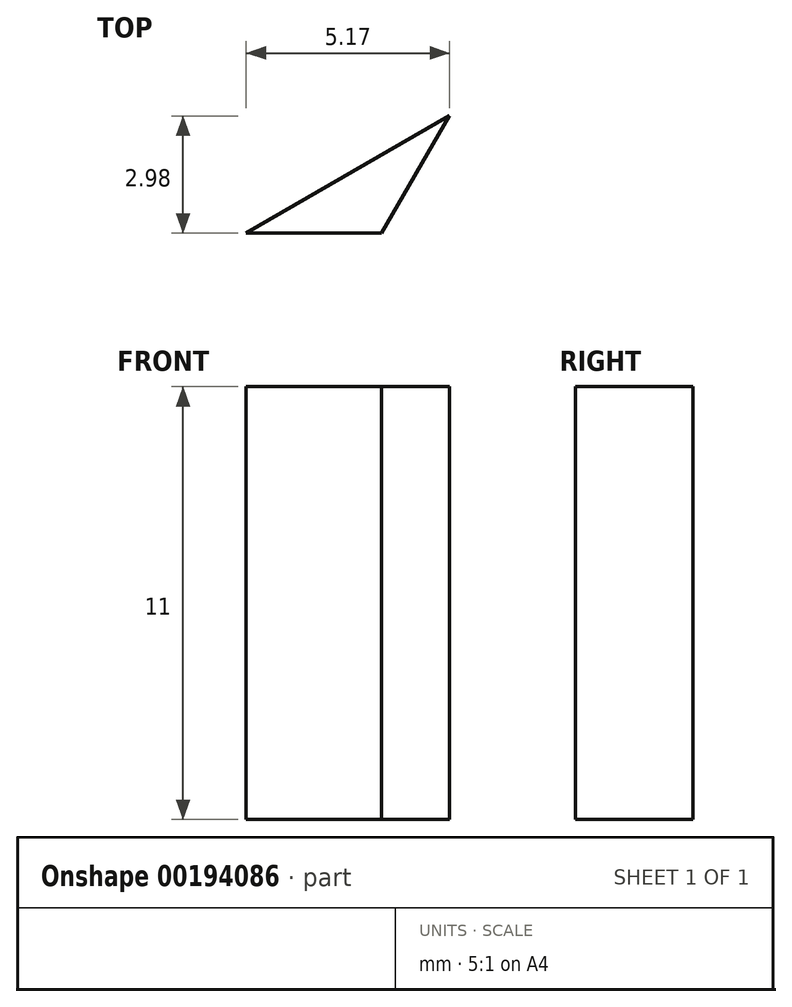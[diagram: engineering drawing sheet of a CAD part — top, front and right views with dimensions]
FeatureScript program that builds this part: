
annotation { "Feature Type Name" : "Feature", "Feature Type Description" : "" }
export const myFeature = defineFeature(function(context is Context, id is Id, definition is map)
    precondition{}
    {
        {
            var Q0;
            Q0=qCreatedBy(makeId("Top.planeOp"),FACE);
            var sketch = newSketch(context, id + "F0", { "sketchPlane" : qUnion([Q0])});
            skLineSegment(sketch, "E0", {"start": v(0, 0) * mm, "end": v(3.45, 0) * mm});
            skLineSegment(sketch, "E1", {"start": v(3.45, 0) * mm, "end": v(0, 0) * mm});
            skLineSegment(sketch, "E2", {"start": v(0, 0) * mm, "end": v(0, 0) * mm});
            skLineSegment(sketch, "E3", {"start": v(-1565.36, 0) * mm, "end": v(-1569.84, -1.45) * mm});
            skLineSegment(sketch, "E4", {"start": v(-1569.84, -1.45) * mm, "end": v(-3139.21, 1.84) * mm});
            skLineSegment(sketch, "E5", {"start": v(-3139.21, 1.84) * mm, "end": v(-4704.9, 2.85) * mm});
            skLineSegment(sketch, "E6", {"start": v(3.45, 0) * mm, "end": v(5.17, 2.98) * mm});
            skLineSegment(sketch, "E7", {"start": v(5.17, 2.98) * mm, "end": v(0, 0) * mm});
            skSolve(sketch);
        }
        {
            var Q0;
            Q0 = qSketchRegion(id + "F0", true);
            extrude(context, id + "F1", {"entities" : qUnion([Q0]), "depth" : 11 * mm});
        }
    });
